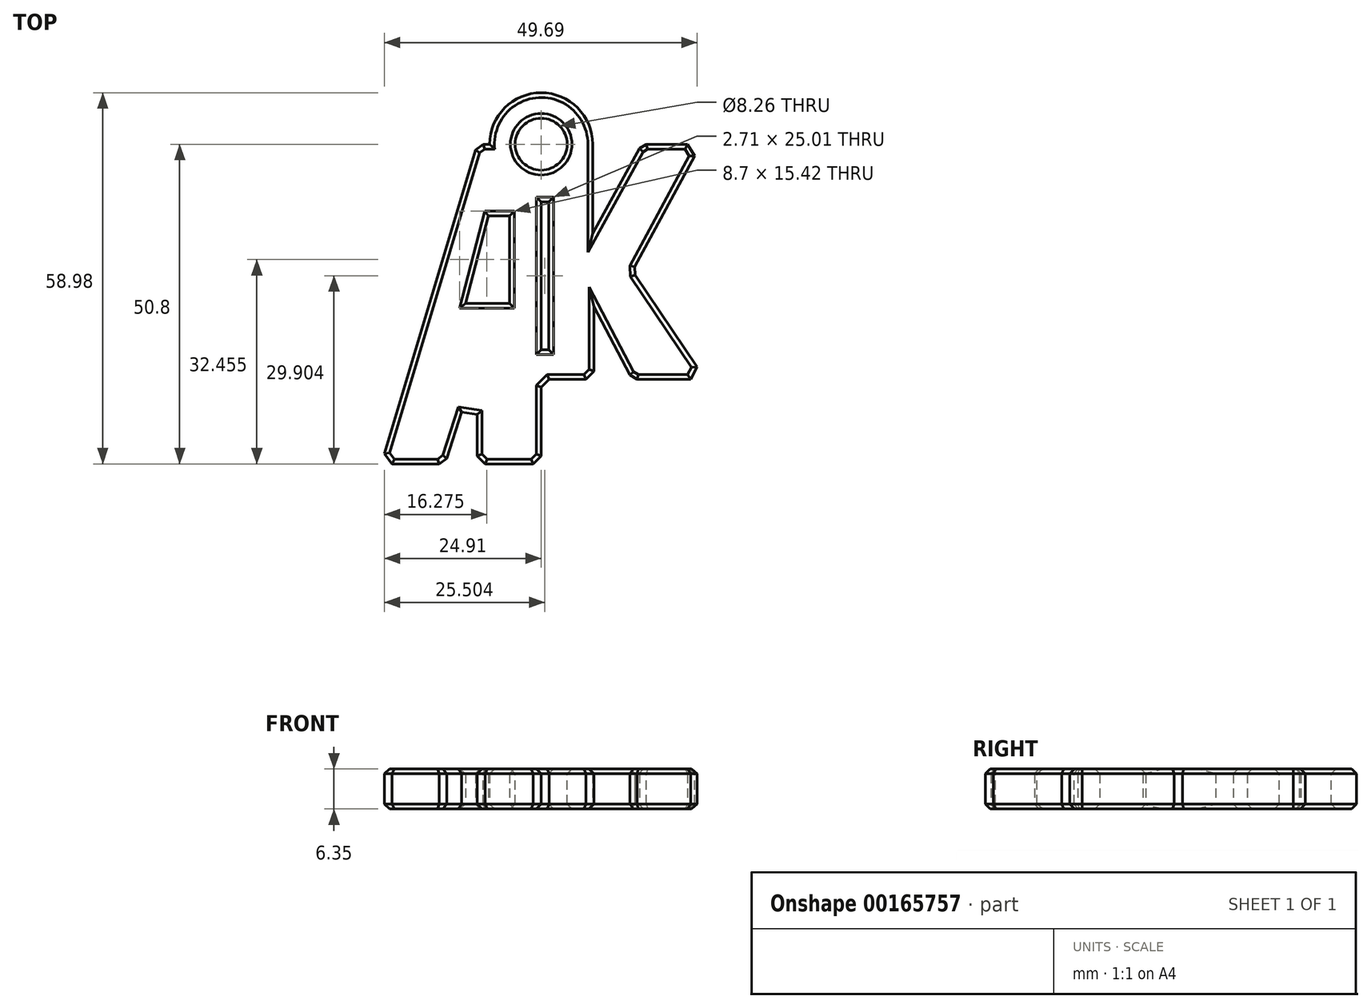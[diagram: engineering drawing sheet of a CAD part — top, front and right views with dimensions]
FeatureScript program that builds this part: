
annotation { "Feature Type Name" : "Feature", "Feature Type Description" : "" }
export const myFeature = defineFeature(function(context is Context, id is Id, definition is map)
    precondition{}
    {
        {
            var Q0;
            Q0=qCreatedBy(makeId("Top.planeOp"),FACE);
            var sketch = newSketch(context, id + "F0", { "sketchPlane" : qUnion([Q0])});
            skLineSegment(sketch, "E0", {"start": v(0, 0) * mm, "end": v(0, 50.8) * mm});
            skLineSegment(sketch, "E1.bottom", {"start": v(0, 50.8) * mm, "end": v(-10.16, 50.8) * mm});
            skLineSegment(sketch, "E1.top", {"start": v(0, 0) * mm, "end": v(-10.16, 0) * mm});
            skLineSegment(sketch, "E1.left", {"start": v(0, 50.8) * mm, "end": v(0, 0) * mm});
            skLineSegment(sketch, "E2", {"start": v(-25.4, 0) * mm, "end": v(-10.16, 50.8) * mm});
            skLineSegment(sketch, "E3", {"start": v(-25.4, 0) * mm, "end": v(-15.24, 0) * mm});
            skLineSegment(sketch, "E4", {"start": v(-10.16, 0) * mm, "end": v(-10.16, 16.08) * mm});
            skLineSegment(sketch, "E5", {"start": v(-10.16, 16.08) * mm, "end": v(-15.24, 0) * mm});
            skLineSegment(sketch, "E6", {"start": v(-8.36, 39.4) * mm, "end": v(-5.05, 39.4) * mm});
            skLineSegment(sketch, "E7", {"start": v(-5.05, 39.4) * mm, "end": v(-5.05, 25.5) * mm});
            skLineSegment(sketch, "E8", {"start": v(-5.05, 25.5) * mm, "end": v(-12, 25.5) * mm});
            skLineSegment(sketch, "E9", {"start": v(-12, 25.5) * mm, "end": v(-8.36, 39.4) * mm});
            skLineSegment(sketch, "E10.trimOffspring", {"start": v(-15.24, 0) * mm, "end": v(-25.4, 0) * mm});
            skLineSegment(sketch, "E11", {"start": v(8.18, 50.8) * mm, "end": v(8.18, 36.59) * mm});
            skLineSegment(sketch, "E12", {"start": v(8.18, 36.59) * mm, "end": v(15.95, 50.8) * mm});
            skLineSegment(sketch, "E13", {"start": v(15.95, 50.8) * mm, "end": v(25.4, 50.8) * mm});
            skLineSegment(sketch, "E14", {"start": v(25.4, 50.8) * mm, "end": v(14.47, 30.64) * mm});
            skLineSegment(sketch, "E15", {"start": v(14.47, 30.64) * mm, "end": v(26.12, 13.44) * mm});
            skLineSegment(sketch, "E16", {"start": v(26.12, 13.44) * mm, "end": v(14.47, 13.44) * mm});
            skLineSegment(sketch, "E17", {"start": v(14.47, 13.44) * mm, "end": v(8.35, 25.01) * mm});
            skLineSegment(sketch, "E18", {"start": v(8.35, 25.01) * mm, "end": v(8.35, 13.44) * mm});
            skLineSegment(sketch, "E19", {"start": v(8.35, 13.44) * mm, "end": v(0, 13.44) * mm});
            skLineSegment(sketch, "E20", {"start": v(0, 50.8) * mm, "end": v(25.4, 50.8) * mm});
            skLineSegment(sketch, "E21.bottom", {"start": v(0, 18.16) * mm, "end": v(1.19, 18.16) * mm});
            skLineSegment(sketch, "E21.top", {"start": v(0, 41.65) * mm, "end": v(1.19, 41.65) * mm});
            skLineSegment(sketch, "E21.left", {"start": v(0, 18.16) * mm, "end": v(0, 41.65) * mm});
            skLineSegment(sketch, "E21.right", {"start": v(1.19, 18.16) * mm, "end": v(1.19, 41.65) * mm});
            skArc(sketch, "E22", {"start": v(8.18, 50.8) * mm, "mid": v(0, 58.98) * mm, "end": v(-8.18, 50.8) * mm});
            skCircle(sketch, "E23", {"center": v(0, 50.8) * mm, "radius": 4.45 * mm});
            skSolve(sketch);
        }
        {
            var Q0;
            {var subQ3=sQuery(id+"F0.wireOp",EDGE,"E2");Q0=makeQuery(id+"F0.imprint","IMPRINT",FACE,{"disambiguationData":[TD([[makeQuery(id+"F0.imprint","IMPRINT",EDGE,{"derivedFrom":subQ3}),-1.0]])]});}
            var Q1;
            {var subQ10=sQuery(id+"F0.wireOp",EDGE,"E11");Q1=makeQuery(id+"F0.imprint","IMPRINT",FACE,{"disambiguationData":[TD([[makeQuery(id+"F0.imprint","IMPRINT",EDGE,{"derivedFrom":subQ10}),-1.0]])]});}
            var Q2;
            {var subQ0=sQuery(id+"F0.wireOp",EDGE,"E22");Q2=makeQuery(id+"F0.imprint","IMPRINT",FACE,{"disambiguationData":[TD([[makeQuery(id+"F0.imprint","IMPRINT",EDGE,{"derivedFrom":subQ0}),1.0]])]});}
            extrude(context, id + "F1", {"entities" : qUnion([Q0, Q1, Q2]), "depth" : 6.35 * mm});
        }
        {
            var Q0;
            Q0=makeQuery(id+"F1.opExtrude","SWEPT_EDGE",EDGE,{"disambiguationData":[OSD([sQuery(id+"F0.wireOp",EDGE,"E14"),sQuery(id+"F0.wireOp",EDGE,"E20")])]});
            var Q1;
            Q1=makeQuery(id+"F1.opExtrude","SWEPT_EDGE",EDGE,{"disambiguationData":[OSD([sQuery(id+"F0.wireOp",EDGE,"E15"),sQuery(id+"F0.wireOp",EDGE,"E16")])]});
            var Q2;
            Q2=makeQuery(id+"F1.opExtrude","SWEPT_EDGE",EDGE,{"disambiguationData":[OSD([sQuery(id+"F0.wireOp",EDGE,"E1.left"),sQuery(id+"F0.wireOp",EDGE,"E1.top")])]});
            var Q3;
            Q3=makeQuery(id+"F1.opExtrude","SWEPT_EDGE",EDGE,{"disambiguationData":[OSD([sQuery(id+"F0.wireOp",EDGE,"E2"),sQuery(id+"F0.wireOp",EDGE,"E10.trimOffspring")])]});
            var Q4;
            Q4=makeQuery(id+"F1.opExtrude","SWEPT_EDGE",EDGE,{"disambiguationData":[OSD([sQuery(id+"F0.wireOp",EDGE,"E1.bottom"),sQuery(id+"F0.wireOp",EDGE,"E2")])]});
            var Q5;
            Q5=makeQuery(id+"F1.opExtrude","SWEPT_EDGE",EDGE,{"disambiguationData":[OSD([sQuery(id+"F0.wireOp",EDGE,"E18"),sQuery(id+"F0.wireOp",EDGE,"E19")])]});
            var Q6;
            Q6=makeQuery(id+"F1.opExtrude","SWEPT_EDGE",EDGE,{"disambiguationData":[OSD([sQuery(id+"F0.wireOp",EDGE,"E5"),sQuery(id+"F0.wireOp",EDGE,"E10.trimOffspring")])]});
            var Q7;
            Q7=makeQuery(id+"F1.opExtrude","SWEPT_EDGE",EDGE,{"disambiguationData":[OSD([sQuery(id+"F0.wireOp",EDGE,"E1.top"),sQuery(id+"F0.wireOp",EDGE,"E4")])]});
            chamfer(context, id + "F2", {"entities" : qUnion([Q0, Q1, Q2, Q3, Q4, Q5, Q6, Q7]), "width" : 1.27 * mm, "tangentPropagation" : true});
        }
        {
            var Q0;
            Q0=makeQuery(id+"F1.opExtrude","SWEPT_EDGE",EDGE,{"disambiguationData":[OSD([sQuery(id+"F0.wireOp",EDGE,"E12"),sQuery(id+"F0.wireOp",EDGE,"E20")])]});
            var Q1;
            Q1=makeQuery(id+"F1.opExtrude","SWEPT_EDGE",EDGE,{"disambiguationData":[OSD([sQuery(id+"F0.wireOp",EDGE,"E16"),sQuery(id+"F0.wireOp",EDGE,"E17")])]});
            chamfer(context, id + "F3", {"entities" : qUnion([Q0, Q1]), "width" : 1.27 * mm, "tangentPropagation" : true});
        }
        {
            var Q0;
            Q0=makeQuery(id+"F1.opExtrude","SWEPT_EDGE",EDGE,{"disambiguationData":[OSD([sQuery(id+"F0.wireOp",EDGE,"E1.left"),sQuery(id+"F0.wireOp",EDGE,"E19")])]});
            chamfer(context, id + "F4", {"entities" : qUnion([Q0]), "width" : 1.27 * mm, "tangentPropagation" : true});
        }
        {
            var Q0;
            Q0=makeQuery(id+"F1.opExtrude","CAP_EDGE",EDGE,{"disambiguationData":[OSD([sQuery(id+"F0.wireOp",EDGE,"E10.trimOffspring")])],"isStart":false});
            var Q1;
            Q1=makeQuery(id+"F1.opExtrude","CAP_EDGE",EDGE,{"disambiguationData":[OSD([sQuery(id+"F0.wireOp",EDGE,"E5")])],"isStart":false});
            var Q2;
            Q2=makeQuery(id+"F1.opExtrude","CAP_EDGE",EDGE,{"disambiguationData":[OSD([sQuery(id+"F0.wireOp",EDGE,"E4")])],"isStart":false});
            var Q3;
            Q3=makeQuery(id+"F1.opExtrude","CAP_EDGE",EDGE,{"disambiguationData":[OSD([sQuery(id+"F0.wireOp",EDGE,"E1.left")])],"isStart":false});
            var Q4;
            Q4=makeQuery(id+"F1.opExtrude","CAP_EDGE",EDGE,{"disambiguationData":[OSD([sQuery(id+"F0.wireOp",EDGE,"E1.top")])],"isStart":false});
            var Q5;
            Q5=makeQuery(id+"F1.opExtrude","CAP_EDGE",EDGE,{"disambiguationData":[OSD([sQuery(id+"F0.wireOp",EDGE,"E19")])],"isStart":false});
            var Q6;
            {var subQ0=sQuery(id+"F0.wireOp",EDGE,"E19");var subQ1=sQuery(id+"F0.wireOp",EDGE,"E1.left");Q6=makeQuery(id+"F4.opChamfer","BLEND_EDGE",EDGE,{"blendedFrom":[makeQuery(id+"F1.opExtrude","SWEPT_EDGE",EDGE,{"disambiguationData":[OSD([subQ1,subQ0])]}),makeQuery(id+"F1.opExtrude","CAP_FACE",FACE,{"disambiguationData":[OSD([sQuery(id+"F0.wireOp",EDGE,"E1.bottom"),subQ1,sQuery(id+"F0.wireOp",EDGE,"E2"),sQuery(id+"F0.wireOp",EDGE,"E1.top"),sQuery(id+"F0.wireOp",EDGE,"E4"),sQuery(id+"F0.wireOp",EDGE,"E5"),sQuery(id+"F0.wireOp",EDGE,"E6"),sQuery(id+"F0.wireOp",EDGE,"E7"),sQuery(id+"F0.wireOp",EDGE,"E8"),sQuery(id+"F0.wireOp",EDGE,"E9"),sQuery(id+"F0.wireOp",EDGE,"E10.trimOffspring"),sQuery(id+"F0.wireOp",EDGE,"E11"),sQuery(id+"F0.wireOp",EDGE,"E12"),sQuery(id+"F0.wireOp",EDGE,"E14"),sQuery(id+"F0.wireOp",EDGE,"E15"),sQuery(id+"F0.wireOp",EDGE,"E16"),sQuery(id+"F0.wireOp",EDGE,"E17"),sQuery(id+"F0.wireOp",EDGE,"E18"),subQ0,sQuery(id+"F0.wireOp",EDGE,"E20"),sQuery(id+"F0.wireOp",EDGE,"w4k5W7gi-v5UZ-TcSr-jvkR-Fowr7DOptpjt"),sQuery(id+"F0.wireOp",EDGE,"E21.bottom"),sQuery(id+"F0.wireOp",EDGE,"E21.top"),sQuery(id+"F0.wireOp",EDGE,"E21.left"),sQuery(id+"F0.wireOp",EDGE,"E21.right"),sQuery(id+"F0.wireOp",EDGE,"E22")])],"isStart":false})],"blendedInto":[makeQuery(id+"F1.opExtrude","CAP_FACE",FACE,{"disambiguationData":[OSD([sQuery(id+"F0.wireOp",EDGE,"E1.bottom"),subQ1,sQuery(id+"F0.wireOp",EDGE,"E2"),sQuery(id+"F0.wireOp",EDGE,"E1.top"),sQuery(id+"F0.wireOp",EDGE,"E4"),sQuery(id+"F0.wireOp",EDGE,"E5"),sQuery(id+"F0.wireOp",EDGE,"E6"),sQuery(id+"F0.wireOp",EDGE,"E7"),sQuery(id+"F0.wireOp",EDGE,"E8"),sQuery(id+"F0.wireOp",EDGE,"E9"),sQuery(id+"F0.wireOp",EDGE,"E10.trimOffspring"),sQuery(id+"F0.wireOp",EDGE,"E11"),sQuery(id+"F0.wireOp",EDGE,"E12"),sQuery(id+"F0.wireOp",EDGE,"E14"),sQuery(id+"F0.wireOp",EDGE,"E15"),sQuery(id+"F0.wireOp",EDGE,"E16"),sQuery(id+"F0.wireOp",EDGE,"E17"),sQuery(id+"F0.wireOp",EDGE,"E18"),subQ0,sQuery(id+"F0.wireOp",EDGE,"E20"),sQuery(id+"F0.wireOp",EDGE,"w4k5W7gi-v5UZ-TcSr-jvkR-Fowr7DOptpjt"),sQuery(id+"F0.wireOp",EDGE,"E21.bottom"),sQuery(id+"F0.wireOp",EDGE,"E21.top"),sQuery(id+"F0.wireOp",EDGE,"E21.left"),sQuery(id+"F0.wireOp",EDGE,"E21.right"),sQuery(id+"F0.wireOp",EDGE,"E22")])],"isStart":false})]});}
            var Q7;
            Q7=makeQuery(id+"F1.opExtrude","CAP_EDGE",EDGE,{"disambiguationData":[OSD([sQuery(id+"F0.wireOp",EDGE,"E18")])],"isStart":false});
            var Q8;
            Q8=makeQuery(id+"F1.opExtrude","CAP_EDGE",EDGE,{"disambiguationData":[OSD([sQuery(id+"F0.wireOp",EDGE,"E17")])],"isStart":false});
            var Q9;
            Q9=makeQuery(id+"F1.opExtrude","CAP_EDGE",EDGE,{"disambiguationData":[OSD([sQuery(id+"F0.wireOp",EDGE,"E16")])],"isStart":false});
            var Q10;
            Q10=makeQuery(id+"F1.opExtrude","CAP_EDGE",EDGE,{"disambiguationData":[OSD([sQuery(id+"F0.wireOp",EDGE,"E15")])],"isStart":false});
            var Q11;
            Q11=makeQuery(id+"F1.opExtrude","CAP_EDGE",EDGE,{"disambiguationData":[OSD([sQuery(id+"F0.wireOp",EDGE,"E14")])],"isStart":false});
            var Q12;
            Q12=makeQuery(id+"F1.opExtrude","CAP_EDGE",EDGE,{"disambiguationData":[OSD([sQuery(id+"F0.wireOp",EDGE,"E20")])],"isStart":false});
            var Q13;
            Q13=makeQuery(id+"F1.opExtrude","CAP_EDGE",EDGE,{"disambiguationData":[OSD([sQuery(id+"F0.wireOp",EDGE,"E12")])],"isStart":false});
            var Q14;
            Q14=makeQuery(id+"F1.opExtrude","CAP_EDGE",EDGE,{"disambiguationData":[OSD([sQuery(id+"F0.wireOp",EDGE,"E11")])],"isStart":false});
            var Q15;
            Q15=makeQuery(id+"F1.opExtrude","CAP_EDGE",EDGE,{"disambiguationData":[OSD([sQuery(id+"F0.wireOp",EDGE,"E22")])],"isStart":false});
            var Q16;
            Q16=makeQuery(id+"F1.opExtrude","CAP_EDGE",EDGE,{"disambiguationData":[OSD([sQuery(id+"F0.wireOp",EDGE,"E2")])],"isStart":false});
            var Q17;
            Q17=makeQuery(id+"F1.opExtrude","CAP_EDGE",EDGE,{"disambiguationData":[OSD([sQuery(id+"F0.wireOp",EDGE,"E1.bottom")])],"isStart":false});
            var Q18;
            Q18=makeQuery(id+"F1.opExtrude","CAP_FACE",FACE,{"disambiguationData":[OSD([sQuery(id+"F0.wireOp",EDGE,"E1.bottom"),sQuery(id+"F0.wireOp",EDGE,"E1.left"),sQuery(id+"F0.wireOp",EDGE,"E2"),sQuery(id+"F0.wireOp",EDGE,"E1.top"),sQuery(id+"F0.wireOp",EDGE,"E4"),sQuery(id+"F0.wireOp",EDGE,"E5"),sQuery(id+"F0.wireOp",EDGE,"E6"),sQuery(id+"F0.wireOp",EDGE,"E7"),sQuery(id+"F0.wireOp",EDGE,"E8"),sQuery(id+"F0.wireOp",EDGE,"E9"),sQuery(id+"F0.wireOp",EDGE,"E10.trimOffspring"),sQuery(id+"F0.wireOp",EDGE,"E11"),sQuery(id+"F0.wireOp",EDGE,"E12"),sQuery(id+"F0.wireOp",EDGE,"E14"),sQuery(id+"F0.wireOp",EDGE,"E15"),sQuery(id+"F0.wireOp",EDGE,"E16"),sQuery(id+"F0.wireOp",EDGE,"E17"),sQuery(id+"F0.wireOp",EDGE,"E18"),sQuery(id+"F0.wireOp",EDGE,"E19"),sQuery(id+"F0.wireOp",EDGE,"E20"),sQuery(id+"F0.wireOp",EDGE,"w4k5W7gi-v5UZ-TcSr-jvkR-Fowr7DOptpjt"),sQuery(id+"F0.wireOp",EDGE,"E21.bottom"),sQuery(id+"F0.wireOp",EDGE,"E21.top"),sQuery(id+"F0.wireOp",EDGE,"E21.left"),sQuery(id+"F0.wireOp",EDGE,"E21.right"),sQuery(id+"F0.wireOp",EDGE,"E22")])],"isStart":false});
            chamfer(context, id + "F5", {"entities" : qUnion([Q0, Q1, Q2, Q3, Q4, Q5, Q6, Q7, Q8, Q9, Q10, Q11, Q12, Q13, Q14, Q15, Q16, Q17, Q18]), "width" : 0.76 * mm, "tangentPropagation" : true});
        }
        {
            var Q0;
            Q0=makeQuery(id+"F1.opExtrude","CAP_FACE",FACE,{"disambiguationData":[OSD([sQuery(id+"F0.wireOp",EDGE,"E1.bottom"),sQuery(id+"F0.wireOp",EDGE,"E1.left"),sQuery(id+"F0.wireOp",EDGE,"E2"),sQuery(id+"F0.wireOp",EDGE,"E1.top"),sQuery(id+"F0.wireOp",EDGE,"E4"),sQuery(id+"F0.wireOp",EDGE,"E5"),sQuery(id+"F0.wireOp",EDGE,"E6"),sQuery(id+"F0.wireOp",EDGE,"E7"),sQuery(id+"F0.wireOp",EDGE,"E8"),sQuery(id+"F0.wireOp",EDGE,"E9"),sQuery(id+"F0.wireOp",EDGE,"E10.trimOffspring"),sQuery(id+"F0.wireOp",EDGE,"E11"),sQuery(id+"F0.wireOp",EDGE,"E12"),sQuery(id+"F0.wireOp",EDGE,"E14"),sQuery(id+"F0.wireOp",EDGE,"E15"),sQuery(id+"F0.wireOp",EDGE,"E16"),sQuery(id+"F0.wireOp",EDGE,"E17"),sQuery(id+"F0.wireOp",EDGE,"E18"),sQuery(id+"F0.wireOp",EDGE,"E19"),sQuery(id+"F0.wireOp",EDGE,"E20"),sQuery(id+"F0.wireOp",EDGE,"w4k5W7gi-v5UZ-TcSr-jvkR-Fowr7DOptpjt"),sQuery(id+"F0.wireOp",EDGE,"E21.bottom"),sQuery(id+"F0.wireOp",EDGE,"E21.top"),sQuery(id+"F0.wireOp",EDGE,"E21.left"),sQuery(id+"F0.wireOp",EDGE,"E21.right"),sQuery(id+"F0.wireOp",EDGE,"E22")])],"isStart":true});
            chamfer(context, id + "F6", {"entities" : qUnion([Q0]), "width" : 0.76 * mm, "tangentPropagation" : true});
        }
        {
            var Q0;
            Q0=makeQuery(id+"F1.opExtrude","CAP_FACE",FACE,{"disambiguationData":[OSD([sQuery(id+"F0.wireOp",EDGE,"E1.bottom"),sQuery(id+"F0.wireOp",EDGE,"E1.left"),sQuery(id+"F0.wireOp",EDGE,"E2"),sQuery(id+"F0.wireOp",EDGE,"E1.top"),sQuery(id+"F0.wireOp",EDGE,"E4"),sQuery(id+"F0.wireOp",EDGE,"E5"),sQuery(id+"F0.wireOp",EDGE,"E6"),sQuery(id+"F0.wireOp",EDGE,"E7"),sQuery(id+"F0.wireOp",EDGE,"E8"),sQuery(id+"F0.wireOp",EDGE,"E9"),sQuery(id+"F0.wireOp",EDGE,"E10.trimOffspring"),sQuery(id+"F0.wireOp",EDGE,"E11"),sQuery(id+"F0.wireOp",EDGE,"E12"),sQuery(id+"F0.wireOp",EDGE,"E14"),sQuery(id+"F0.wireOp",EDGE,"E15"),sQuery(id+"F0.wireOp",EDGE,"E16"),sQuery(id+"F0.wireOp",EDGE,"E17"),sQuery(id+"F0.wireOp",EDGE,"E18"),sQuery(id+"F0.wireOp",EDGE,"E19"),sQuery(id+"F0.wireOp",EDGE,"E20"),sQuery(id+"F0.wireOp",EDGE,"E21.bottom"),sQuery(id+"F0.wireOp",EDGE,"E21.top"),sQuery(id+"F0.wireOp",EDGE,"E21.left"),sQuery(id+"F0.wireOp",EDGE,"E21.right"),sQuery(id+"F0.wireOp",EDGE,"E22"),sQuery(id+"F0.wireOp",EDGE,"E23")])],"isStart":false});
            var sketch = newSketch(context, id + "F7", { "sketchPlane" : qUnion([Q0])});
            skCircle(sketch, "E24", {"center": v(0, 50.8) * mm, "radius": 5.85 * mm});
            skCircle(sketch, "E25", {"center": v(0, 50.8) * mm, "radius": 1.95 * mm});
            skCircle(sketch, "E26", {"center": v(0, 50.8) * mm, "radius": 4.13 * mm});
            skSolve(sketch);
        }
        {
            var Q0;
            Q0=makeQuery(id+"F7.imprint","IMPRINT",FACE,{"disambiguationData":[TD([[makeQuery(id+"F7.imprint","IMPRINT",EDGE,{"derivedFrom":sQuery(id+"F7.wireOp",EDGE,"E26")}),-1.0]])]});
            extrude(context, id + "F8", {"entities" : qUnion([Q0]), "operationType" : NewBodyOperationType.ADD, "oppositeDirection" : true, "depth" : 6.35 * mm});
        }
        {
            var Q0;
            Q0=makeQuery(id+"F8.opExtrude","CAP_EDGE",EDGE,{"disambiguationData":[OSD([sQuery(id+"F7.wireOp",EDGE,"E26")])],"isStart":true});
            var Q1;
            Q1=makeQuery(id+"F8.opExtrude","CAP_EDGE",EDGE,{"disambiguationData":[OSD([sQuery(id+"F7.wireOp",EDGE,"E26")])],"isStart":false});
            chamfer(context, id + "F9", {"entities" : qUnion([Q0, Q1]), "width" : 0.76 * mm, "tangentPropagation" : true});
        }
    });
